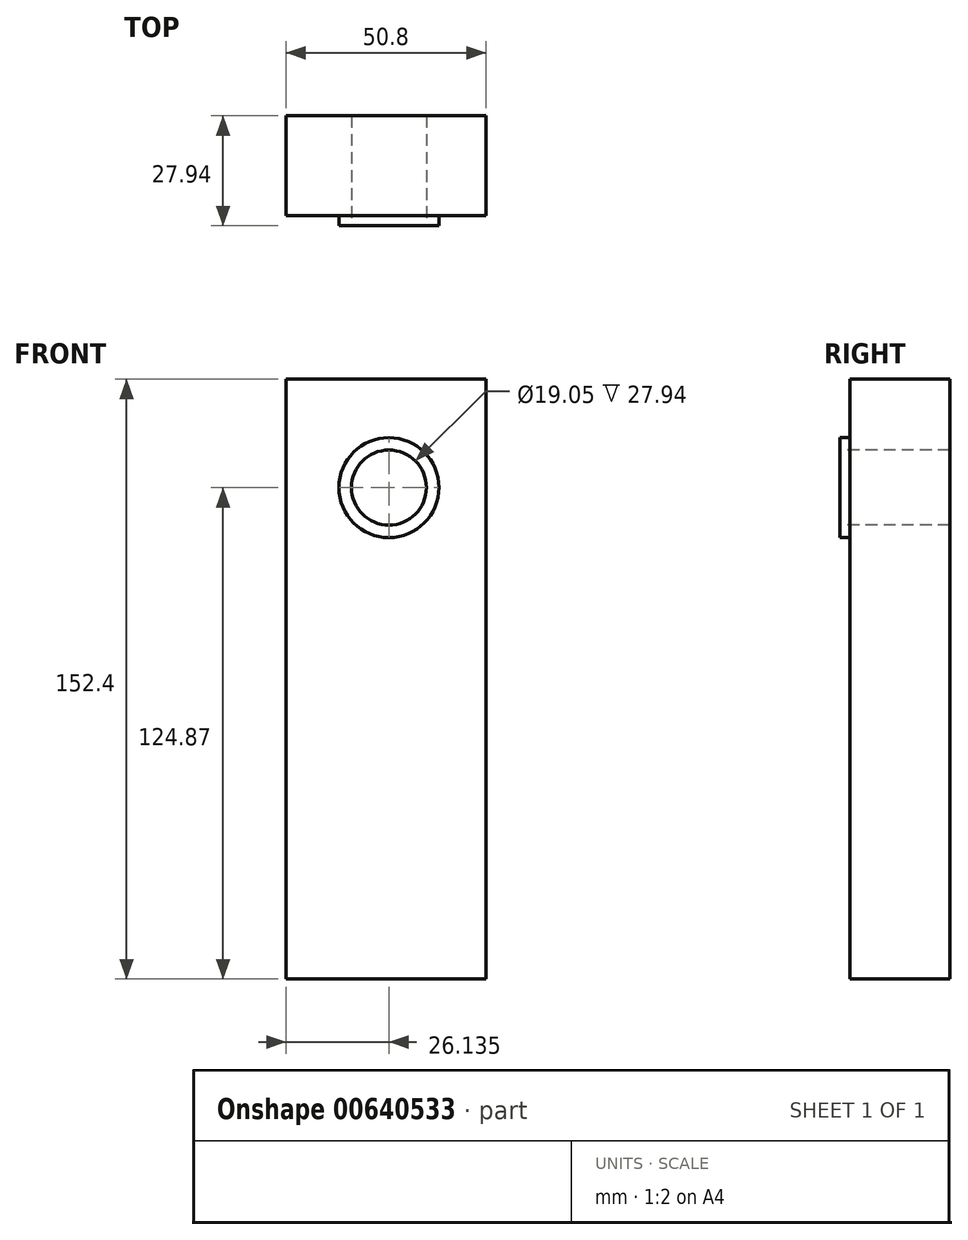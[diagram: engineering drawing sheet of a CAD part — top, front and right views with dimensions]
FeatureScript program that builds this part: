
annotation { "Feature Type Name" : "Feature", "Feature Type Description" : "" }
export const myFeature = defineFeature(function(context is Context, id is Id, definition is map)
    precondition{}
    {
        {
            var Q0;
            Q0=qCreatedBy(makeId("Top.planeOp"),FACE);
            var sketch = newSketch(context, id + "F0", { "sketchPlane" : qUnion([Q0])});
            skLineSegment(sketch, "E0.bottom", {"start": v(-50.8, 0) * mm, "end": v(0, 0) * mm});
            skLineSegment(sketch, "E0.top", {"start": v(-50.8, -25.4) * mm, "end": v(0, -25.4) * mm});
            skLineSegment(sketch, "E0.left", {"start": v(-50.8, 0) * mm, "end": v(-50.8, -25.4) * mm});
            skLineSegment(sketch, "E0.right", {"start": v(0, 0) * mm, "end": v(0, -25.4) * mm});
            skSolve(sketch);
        }
        {
            var Q0;
            Q0=makeQuery(id+"F0.imprint","IMPRINT",FACE,{"disambiguationData":[TD([[makeQuery(id+"F0.imprint","IMPRINT",EDGE,{"derivedFrom":sQuery(id+"F0.wireOp",EDGE,"E0.bottom")}),-1.0]])]});
            extrude(context, id + "F1", {"entities" : qUnion([Q0]), "depth" : 152.4 * mm, "offsetDistance" : 25.4 * mm});
        }
        {
            var Q0;
            Q0=makeQuery(id+"F1.opExtrude","SWEPT_FACE",FACE,{"disambiguationData":[OSD([sQuery(id+"F0.wireOp",EDGE,"E0.top")])]});
            var sketch = newSketch(context, id + "F2", { "sketchPlane" : qUnion([Q0])});
            skCircle(sketch, "E1", {"center": v(-24.66, 124.87) * mm, "radius": 9.53 * mm});
            skSolve(sketch);
        }
        {
            var Q0;
            Q0 = qSketchRegion(id + "F2", true);
            extrude(context, id + "F3", {"entities" : qUnion([Q0]), "operationType" : NewBodyOperationType.REMOVE, "oppositeDirection" : true, "depth" : 25.4 * mm, "offsetDistance" : 25.4 * mm});
        }
        {
            var Q0;
            Q0=makeQuery(id+"F1.opExtrude","SWEPT_FACE",FACE,{"disambiguationData":[OSD([sQuery(id+"F0.wireOp",EDGE,"E0.top")])]});
            var sketch = newSketch(context, id + "F4", { "sketchPlane" : qUnion([Q0])});
            skCircle(sketch, "E2", {"center": v(-24.66, 124.87) * mm, "radius": 12.7 * mm});
            skSolve(sketch);
        }
        {
            var Q0;
            Q0=makeQuery(id+"F4.imprint","IMPRINT",FACE,{"disambiguationData":[TD([[makeQuery(id+"F4.imprint","IMPRINT",EDGE,{"derivedFrom":sQuery(id+"F4.wireOp",EDGE,"E2")}),1.0]])]});
            extrude(context, id + "F5", {"entities" : qUnion([Q0]), "operationType" : NewBodyOperationType.ADD, "depth" : 2.54 * mm, "offsetDistance" : 25.4 * mm});
        }
    });
